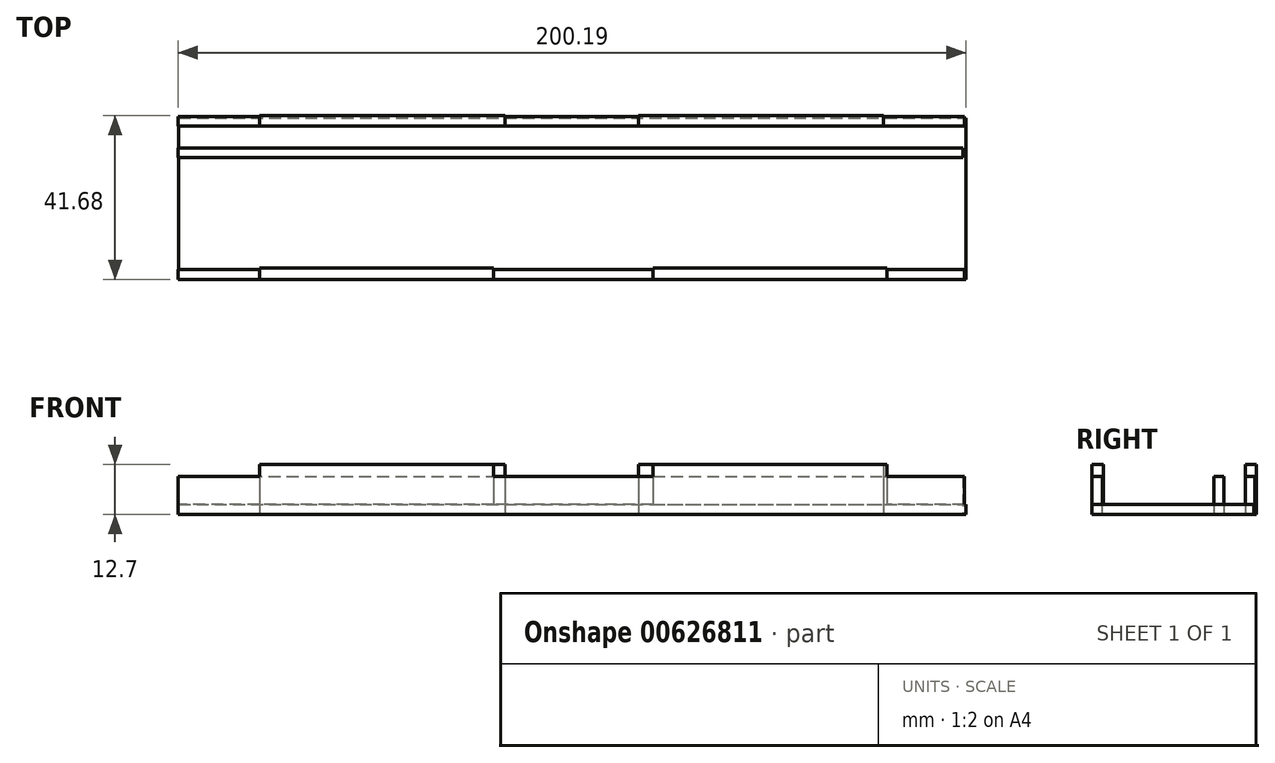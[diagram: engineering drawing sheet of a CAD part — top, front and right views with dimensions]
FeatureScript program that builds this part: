
annotation { "Feature Type Name" : "Feature", "Feature Type Description" : "" }
export const myFeature = defineFeature(function(context is Context, id is Id, definition is map)
    precondition{}
    {
        {
            var Q0;
            Q0=qCreatedBy(makeId("Top.planeOp"),FACE);
            var sketch = newSketch(context, id + "F0", { "sketchPlane" : qUnion([Q0])});
            skLineSegment(sketch, "E0.bottom", {"start": v(-61.23, 41.07) * mm, "end": v(138.8, 41.07) * mm});
            skLineSegment(sketch, "E0.top", {"start": v(-61.23, 0) * mm, "end": v(138.8, 0) * mm});
            skLineSegment(sketch, "E0.left", {"start": v(-61.23, 41.07) * mm, "end": v(-61.23, 0) * mm});
            skLineSegment(sketch, "E0.right", {"start": v(138.8, 41.07) * mm, "end": v(138.8, 0) * mm});
            skSolve(sketch);
        }
        {
            var Q0;
            Q0=qCreatedBy(makeId("Top.planeOp"),FACE);
            var sketch = newSketch(context, id + "F1", { "sketchPlane" : qUnion([Q0])});
            skLineSegment(sketch, "E1.bottom", {"start": v(-61.39, 41.38) * mm, "end": v(138.33, 41.38) * mm});
            skLineSegment(sketch, "E1.top", {"start": v(-61.39, 38.94) * mm, "end": v(138.33, 38.94) * mm});
            skLineSegment(sketch, "E1.left", {"start": v(-61.39, 41.38) * mm, "end": v(-61.39, 38.94) * mm});
            skLineSegment(sketch, "E1.right", {"start": v(138.33, 41.38) * mm, "end": v(138.33, 38.94) * mm});
            skSolve(sketch);
        }
        {
            var Q0;
            Q0 = qSketchRegion(id + "F1", true);
            extrude(context, id + "F2", {"entities" : qUnion([Q0]), "depth" : 9.7 * mm, "offsetDistance" : 25.4 * mm});
        }
        {
            var Q0;
            Q0=qCreatedBy(makeId("Top.planeOp"),FACE);
            var sketch = newSketch(context, id + "F3", { "sketchPlane" : qUnion([Q0])});
            skLineSegment(sketch, "E2.bottom", {"start": v(-40.68, 41.68) * mm, "end": v(21.62, 41.68) * mm});
            skLineSegment(sketch, "E2.top", {"start": v(-40.68, 38.94) * mm, "end": v(21.62, 38.94) * mm});
            skLineSegment(sketch, "E2.left", {"start": v(-40.68, 41.68) * mm, "end": v(-40.68, 38.94) * mm});
            skLineSegment(sketch, "E2.right", {"start": v(21.62, 41.68) * mm, "end": v(21.62, 38.94) * mm});
            skLineSegment(sketch, "E3.bottom", {"start": v(117.81, 41.68) * mm, "end": v(55.51, 41.68) * mm});
            skLineSegment(sketch, "E3.top", {"start": v(117.81, 38.94) * mm, "end": v(55.51, 38.94) * mm});
            skLineSegment(sketch, "E3.left", {"start": v(117.81, 41.68) * mm, "end": v(117.81, 38.94) * mm});
            skLineSegment(sketch, "E3.right", {"start": v(55.51, 41.68) * mm, "end": v(55.51, 38.94) * mm});
            skSolve(sketch);
        }
        {
            var Q0;
            Q0 = qSketchRegion(id + "F3", true);
            extrude(context, id + "F4", {"entities" : qUnion([Q0]), "operationType" : NewBodyOperationType.ADD, "depth" : 12.7 * mm, "offsetDistance" : 25.4 * mm});
        }
        {
            var Q0;
            Q0=qCreatedBy(makeId("Top.planeOp"),FACE);
            var sketch = newSketch(context, id + "F5", { "sketchPlane" : qUnion([Q0])});
            skLineSegment(sketch, "E4.bottom", {"start": v(-61.39, 33.44) * mm, "end": v(138.03, 33.44) * mm});
            skLineSegment(sketch, "E4.top", {"start": v(-61.39, 31) * mm, "end": v(138.03, 31) * mm});
            skLineSegment(sketch, "E4.left", {"start": v(-61.39, 33.44) * mm, "end": v(-61.39, 31) * mm});
            skLineSegment(sketch, "E4.right", {"start": v(138.03, 33.44) * mm, "end": v(138.03, 31) * mm});
            skSolve(sketch);
        }
        {
            var Q0;
            Q0 = qSketchRegion(id + "F5", true);
            extrude(context, id + "F6", {"entities" : qUnion([Q0]), "depth" : 9.68 * mm, "offsetDistance" : 25.4 * mm});
        }
        {
            var Q0;
            Q0=makeQuery(id+"F0.imprint","IMPRINT",FACE,{"disambiguationData":[TD([[makeQuery(id+"F0.imprint","IMPRINT",EDGE,{"derivedFrom":sQuery(id+"F0.wireOp",EDGE,"E0.bottom")}),-1.0]])]});
            extrude(context, id + "F7", {"entities" : qUnion([Q0]), "depth" : 2.5 * mm, "offsetDistance" : 25.4 * mm});
        }
        {
            var Q0;
            Q0=makeQuery(id+"F2.opExtrude","SWEPT_BODY",BODY,{"disambiguationData":[OSD([sQuery(id+"F1.wireOp",EDGE,"E1.bottom"),sQuery(id+"F1.wireOp",EDGE,"E1.top"),sQuery(id+"F1.wireOp",EDGE,"E1.left"),sQuery(id+"F1.wireOp",EDGE,"E1.right")])]});
            var Q1;
            Q1=qCreatedBy(makeId("Front.planeOp"),FACE);
            mirror(context, id + "F8", {"entities" : qUnion([Q0]), "mirrorPlane" : qUnion([Q1])});
        }
        {
            var Q0;
            Q0=makeQuery(id+"F8.opPattern","COPY",BODY,{"derivedFrom":makeQuery(id+"F2.opExtrude","SWEPT_BODY",BODY,{"disambiguationData":[OSD([sQuery(id+"F1.wireOp",EDGE,"E1.bottom"),sQuery(id+"F1.wireOp",EDGE,"E1.top"),sQuery(id+"F1.wireOp",EDGE,"E1.left"),sQuery(id+"F1.wireOp",EDGE,"E1.right")])]}),"instanceName":"1"});
            deleteBodies(context, id + "F9", {"entities" : qUnion([Q0])});
        }
        {
            var Q0;
            Q0=qCreatedBy(makeId("Top.planeOp"),FACE);
            var sketch = newSketch(context, id + "F10", { "sketchPlane" : qUnion([Q0])});
            skLineSegment(sketch, "E5.bottom", {"start": v(-61.39, 0) * mm, "end": v(138.33, 0) * mm});
            skLineSegment(sketch, "E5.top", {"start": v(-61.39, 2.6) * mm, "end": v(138.33, 2.6) * mm});
            skLineSegment(sketch, "E5.left", {"start": v(-61.39, 0) * mm, "end": v(-61.39, 2.6) * mm});
            skLineSegment(sketch, "E5.right", {"start": v(138.33, 0) * mm, "end": v(138.33, 2.6) * mm});
            skSolve(sketch);
        }
        {
            var Q0;
            Q0 = qSketchRegion(id + "F10", true);
            extrude(context, id + "F11", {"entities" : qUnion([Q0]), "operationType" : NewBodyOperationType.ADD, "depth" : 9.68 * mm, "offsetDistance" : 25.4 * mm});
        }
        {
            var Q0;
            Q0=qCreatedBy(makeId("Top.planeOp"),FACE);
            var sketch = newSketch(context, id + "F12", { "sketchPlane" : qUnion([Q0])});
            skLineSegment(sketch, "E6.bottom", {"start": v(-40.73, 2.87) * mm, "end": v(18.68, 2.87) * mm});
            skLineSegment(sketch, "E6.top", {"start": v(-40.73, 0) * mm, "end": v(18.68, 0) * mm});
            skLineSegment(sketch, "E6.left", {"start": v(-40.73, 2.87) * mm, "end": v(-40.73, 0) * mm});
            skLineSegment(sketch, "E6.right", {"start": v(18.68, 2.87) * mm, "end": v(18.68, 0) * mm});
            skLineSegment(sketch, "E7.bottom", {"start": v(118.65, 2.87) * mm, "end": v(59.25, 2.87) * mm});
            skLineSegment(sketch, "E7.top", {"start": v(118.65, 0) * mm, "end": v(59.25, 0) * mm});
            skLineSegment(sketch, "E7.left", {"start": v(118.65, 2.87) * mm, "end": v(118.65, 0) * mm});
            skLineSegment(sketch, "E7.right", {"start": v(59.25, 2.87) * mm, "end": v(59.25, 0) * mm});
            skSolve(sketch);
        }
        {
            var Q0;
            Q0 = qSketchRegion(id + "F12", true);
            extrude(context, id + "F13", {"entities" : qUnion([Q0]), "operationType" : NewBodyOperationType.ADD, "depth" : 12.7 * mm, "offsetDistance" : 25.4 * mm});
        }
    });
